# Revit family: LZPT24
name_source: partatom
category: Lighting Fixtures
units: mm (PartAtom-declared; Revit-internal decimal feet)

## family parameters
Cut with Voids When Loaded = No
Host = Face
Light Source = Yes
OmniClass Number = 23.80.70.11
OmniClass Title = Luminaries for Internal Lighting
Part Type = Normal
Room Calculation Point = No
Round Connector Dimension = Use Diameter
Shared = No

## types (3) — shared parameters
Color Filter = 16777215
Default Elevation = 48 "
Description = LED Zero Plenum® Troffer
Dimming Lamp Color Temperature Shift = <None>
Emit Shape Visible in Rendering = No
Emit from Rectangle Length = 47 "
Emit from Rectangle Width = 23 "
Is 120V = No
Is 277V = Yes
Lamp = LED Lamp
Load Classification = Lighting
Manufacturer = Columbia Lighting
Material Finish = Paint - White
Model = LZPT 24
Opal lens = Glass
Tilt Angle = -90.00°
URL = https://www.currentlighting.com
Voltage = 277 V
Wattage Comments = 26W-92W
zzLength1 = 5.625 "

## per-type parameters (varying)
| type | Apparent Load | Photometric Web File | Watts |
| LZPT24-35HLG-LSRS-EU | 57 VA | LZPT24-35HLG-LSRS-EU.ies | 57 W |
| LZPT24-35LWG-LSRS-EU | 43 VA | LZPT24-35LWG-LSRS-EU.ies | 43 W |
| LZPT24-35MLG-LSRS-EU | 48 VA | LZPT24-35MLG-LSRS-EU.ies | 48 W |

## geometry (parser evidence)
native form markers: Sweep x3
no freeform markers — native parametric forms only
